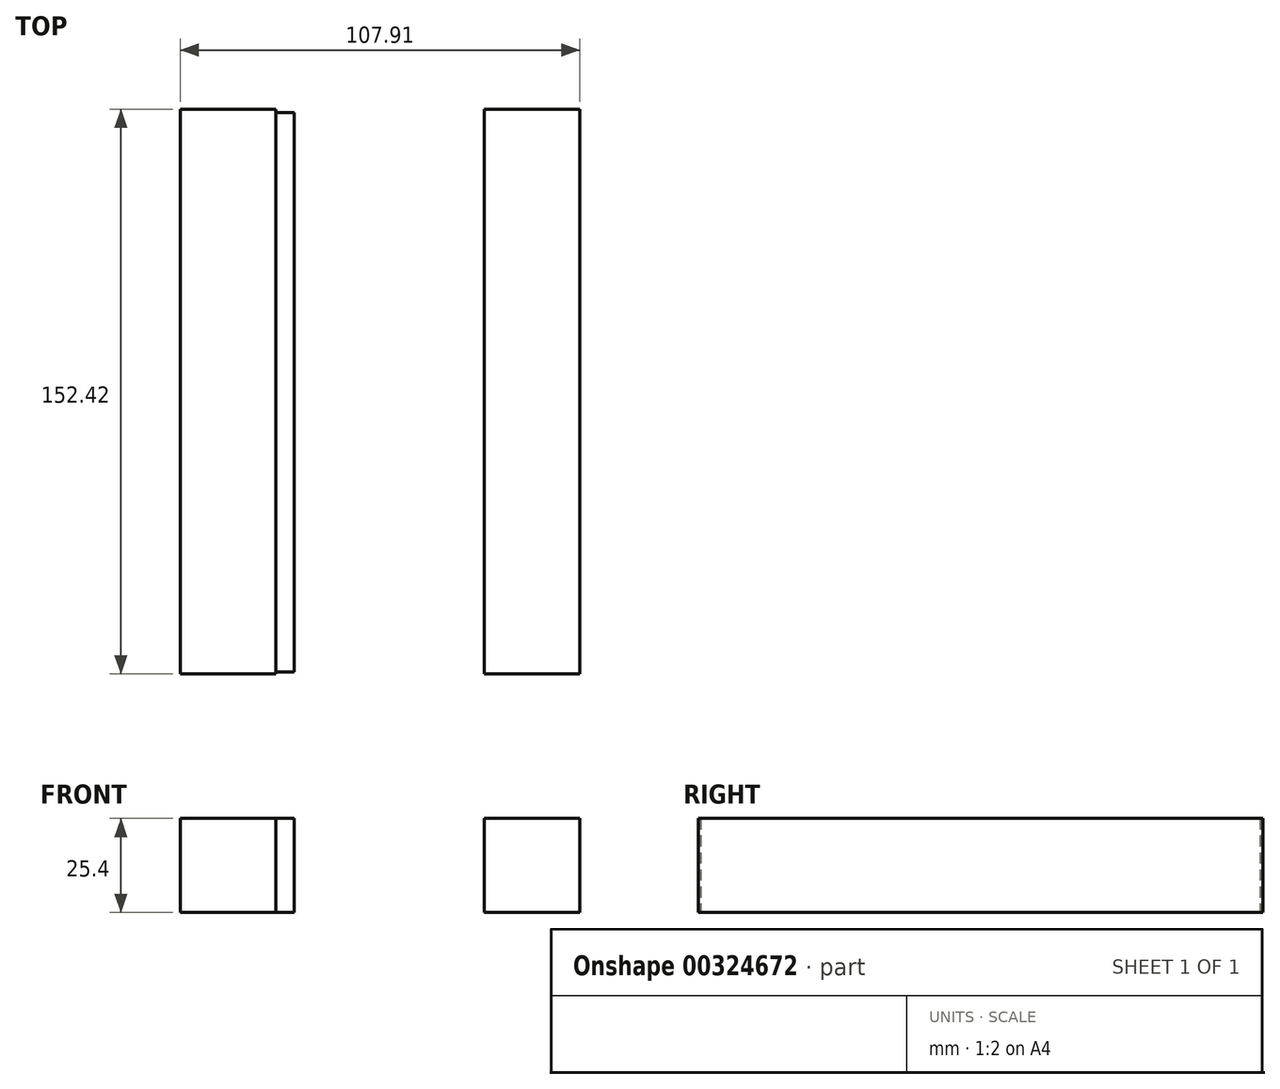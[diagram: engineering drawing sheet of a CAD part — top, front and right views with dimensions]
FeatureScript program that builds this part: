
annotation { "Feature Type Name" : "Feature", "Feature Type Description" : "" }
export const myFeature = defineFeature(function(context is Context, id is Id, definition is map)
    precondition{}
    {
        {
            var Q0;
            Q0=qCreatedBy(makeId("Top.planeOp"),FACE);
            var sketch = newSketch(context, id + "F0", { "sketchPlane" : qUnion([Q0])});
            skLineSegment(sketch, "E0.bottom", {"start": v(-75.93, 76.07) * mm, "end": v(-50.06, 76.07) * mm});
            skLineSegment(sketch, "E0.top", {"start": v(-75.93, -76.35) * mm, "end": v(-50.06, -76.35) * mm});
            skLineSegment(sketch, "E0.left", {"start": v(-75.93, 76.07) * mm, "end": v(-75.93, -76.35) * mm});
            skLineSegment(sketch, "E0.right", {"start": v(-50.06, 76.07) * mm, "end": v(-50.06, -76.35) * mm});
            skSolve(sketch);
        }
        {
            var Q0;
            Q0=makeQuery(id+"F0.imprint","IMPRINT",FACE,{"disambiguationData":[TD([[makeQuery(id+"F0.imprint","IMPRINT",EDGE,{"derivedFrom":sQuery(id+"F0.wireOp",EDGE,"E0.bottom")}),-1.0]])]});
            extrude(context, id + "F1", {"entities" : qUnion([Q0]), "depth" : 25.4 * mm});
        }
        {
            var Q0;
            Q0=makeQuery(id+"F1.opExtrude","SWEPT_BODY",BODY,{"disambiguationData":[OSD([sQuery(id+"F0.wireOp",EDGE,"E0.bottom"),sQuery(id+"F0.wireOp",EDGE,"E0.top"),sQuery(id+"F0.wireOp",EDGE,"E0.left"),sQuery(id+"F0.wireOp",EDGE,"E0.right")])]});
            transform(context, id + "F2", {"entities" : qUnion([Q0]), "transformType" : TransformType.TRANSLATION_3D, "dx" : 82.04 * mm, "dy" : 0 * mm, "dz" : 0 * mm, "makeCopy" : true});
        }
        {
            var Q0;
            Q0=makeQuery(id+"F2.opPattern","COPY",BODY,{"derivedFrom":makeQuery(id+"F1.opExtrude","SWEPT_BODY",BODY,{"disambiguationData":[OSD([sQuery(id+"F0.wireOp",EDGE,"E0.bottom"),sQuery(id+"F0.wireOp",EDGE,"E0.top"),sQuery(id+"F0.wireOp",EDGE,"E0.left"),sQuery(id+"F0.wireOp",EDGE,"E0.right")])]}),"instanceName":"1"});
            transform(context, id + "F3", {"entities" : qUnion([Q0]), "transformType" : TransformType.TRANSLATION_3D, "dx" : -56.64 * mm, "dy" : 0 * mm, "dz" : 0 * mm, "makeCopy" : true});
        }
        {
            var Q0;
            Q0=qCreatedBy(makeId("Top.planeOp"),FACE);
            var sketch = newSketch(context, id + "F4", { "sketchPlane" : qUnion([Q0])});
            skLineSegment(sketch, "E1.bottom", {"start": v(-24.75, 75.23) * mm, "end": v(-19.69, 75.23) * mm});
            skLineSegment(sketch, "E1.top", {"start": v(-24.75, -75.8) * mm, "end": v(-19.69, -75.8) * mm});
            skLineSegment(sketch, "E1.left", {"start": v(-24.75, 75.23) * mm, "end": v(-24.75, -75.8) * mm});
            skLineSegment(sketch, "E1.right", {"start": v(-19.69, 75.23) * mm, "end": v(-19.69, -75.8) * mm});
            skSolve(sketch);
        }
        {
            var Q0;
            Q0=makeQuery(id+"F3.opPattern","COPY",BODY,{"derivedFrom":makeQuery(id+"F2.opPattern","COPY",BODY,{"derivedFrom":makeQuery(id+"F1.opExtrude","SWEPT_BODY",BODY,{"disambiguationData":[OSD([sQuery(id+"F0.wireOp",EDGE,"E0.bottom"),sQuery(id+"F0.wireOp",EDGE,"E0.top"),sQuery(id+"F0.wireOp",EDGE,"E0.left"),sQuery(id+"F0.wireOp",EDGE,"E0.right")])]}),"instanceName":"1"}),"instanceName":"1"});
            deleteBodies(context, id + "F5", {"entities" : qUnion([Q0])});
        }
        {
            var Q0;
            Q0=makeQuery(id+"F4.imprint","IMPRINT",FACE,{"disambiguationData":[TD([[makeQuery(id+"F4.imprint","IMPRINT",EDGE,{"derivedFrom":sQuery(id+"F4.wireOp",EDGE,"E1.bottom")}),-1.0]])]});
            extrude(context, id + "F6", {"entities" : qUnion([Q0]), "depth" : 25.4 * mm});
        }
        {
            var Q0;
            Q0=makeQuery(id+"F6.opExtrude","SWEPT_BODY",BODY,{"disambiguationData":[OSD([sQuery(id+"F4.wireOp",EDGE,"E1.bottom"),sQuery(id+"F4.wireOp",EDGE,"E1.top"),sQuery(id+"F4.wireOp",EDGE,"E1.left"),sQuery(id+"F4.wireOp",EDGE,"E1.right")])]});
            transform(context, id + "F7", {"entities" : qUnion([Q0]), "transformType" : TransformType.TRANSLATION_3D, "dx" : -25.4 * mm, "dy" : 0 * mm, "dz" : 0 * mm, "makeCopy" : true});
        }
        {
            var Q0;
            Q0=makeQuery(id+"F6.opExtrude","SWEPT_BODY",BODY,{"disambiguationData":[OSD([sQuery(id+"F4.wireOp",EDGE,"E1.bottom"),sQuery(id+"F4.wireOp",EDGE,"E1.top"),sQuery(id+"F4.wireOp",EDGE,"E1.left"),sQuery(id+"F4.wireOp",EDGE,"E1.right")])]});
            deleteBodies(context, id + "F8", {"entities" : qUnion([Q0])});
        }
    });
